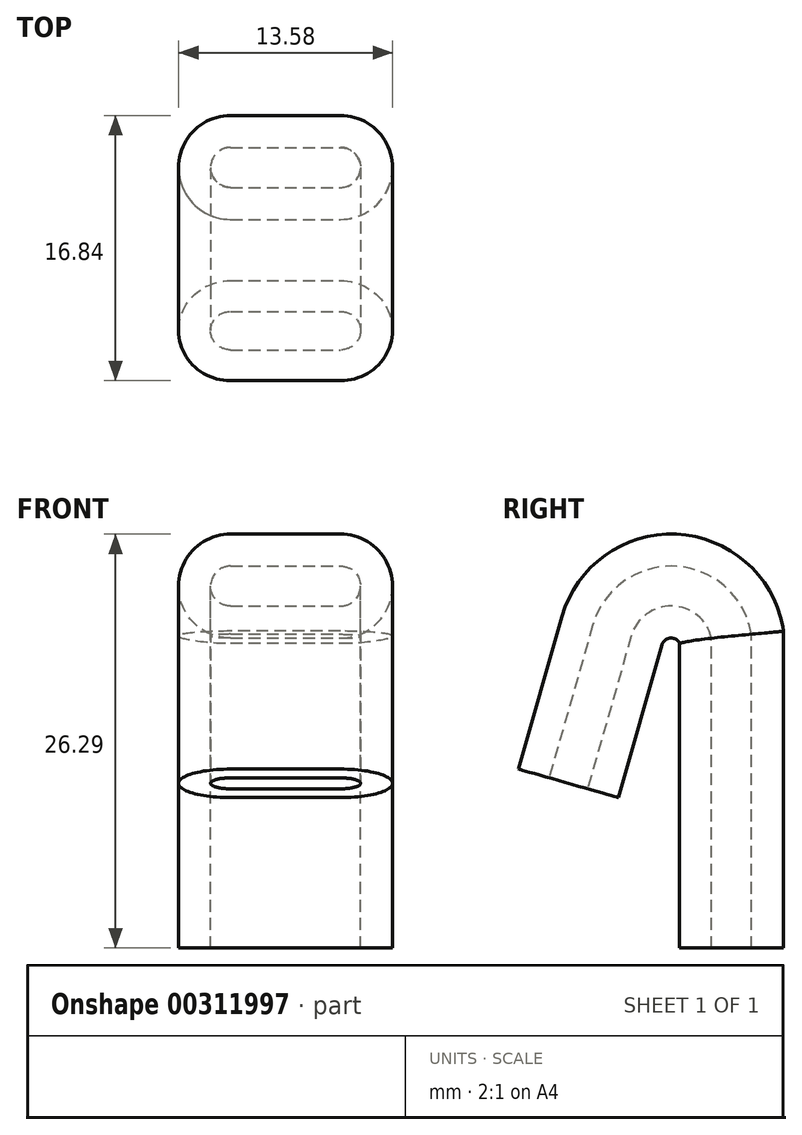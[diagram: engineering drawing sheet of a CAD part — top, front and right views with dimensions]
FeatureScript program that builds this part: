
annotation { "Feature Type Name" : "Feature", "Feature Type Description" : "" }
export const myFeature = defineFeature(function(context is Context, id is Id, definition is map)
    precondition{}
    {
        {
            var Q0;
            Q0=qCreatedBy(makeId("Right.planeOp"),FACE);
            var sketch = newSketch(context, id + "F0", { "sketchPlane" : qUnion([Q0])});
            skLineSegment(sketch, "E0", {"start": v(0, 0) * mm, "end": v(0, 19.81) * mm});
            skLineSegment(sketch, "E1", {"start": v(-5.08, 24.9) * mm, "end": v(-7.6, 24.9) * mm});
            skLineSegment(sketch, "E2", {"start": v(-12.48, 21.2) * mm, "end": v(-15.24, 11.54) * mm});
            skPoint(sketch, "E3.visualSharp", {"position": v(-11.43, 24.9) * mm});
            skArc(sketch, "E3.filletArc", {"start": v(-7.6, 24.9) * mm, "mid": v(-10.66, 23.87) * mm, "end": v(-12.48, 21.2) * mm});
            skPoint(sketch, "E4.visualSharp", {"position": v(0, 24.9) * mm});
            skArc(sketch, "E4.filletArc", {"start": v(0, 19.81) * mm, "mid": v(-1.49, 23.4) * mm, "end": v(-5.08, 24.9) * mm});
            skLineSegment(sketch, "E5.0", {"start": v(-10.14, 20.15) * mm, "end": v(-12.9, 10.46) * mm});
            skLineSegment(sketch, "E6.0", {"start": v(-2.54, 0) * mm, "end": v(-2.54, 19.81) * mm});
            skPoint(sketch, "E7.visualSharp", {"position": v(-9.56, 22.17) * mm});
            skPoint(sketch, "E8.visualSharp", {"position": v(-2.54, 22.35) * mm});
            skArc(sketch, "E9", {"start": v(-2.54, 19.81) * mm, "mid": v(-6.2, 22.99) * mm, "end": v(-10.14, 20.15) * mm});
            skSolve(sketch);
        }
        {
            var Q0;
            Q0=sQuery(id+"F0.wireOp",EDGE,"E6.0");
            var Q1;
            Q1=sQuery(id+"F0.wireOp",VERTEX,"E6.0.start");
            cPlane(context, id + "F1", {"entities" : qUnion([Q0, Q1]), "cplaneType" : CPlaneType.LINE_POINT, "offset" : 25.4 * mm, "width" : 152.4 * mm, "height" : 152.4 * mm});
        }
        {
            var Q0;
            Q0=qCreatedBy(id+"F1.planeOp",FACE);
            var sketch = newSketch(context, id + "F2", { "sketchPlane" : qUnion([Q0])});
            skLineSegment(sketch, "E10.bottom", {"start": v(-3.5, -3.81) * mm, "end": v(3.5, -3.81) * mm});
            skLineSegment(sketch, "E10.top", {"start": v(-3.5, -1.27) * mm, "end": v(3.5, -1.27) * mm});
            skLineSegment(sketch, "E10.left", {"start": v(-4.76, -2.54) * mm, "end": v(-4.76, -2.54) * mm});
            skLineSegment(sketch, "E10.right", {"start": v(4.76, -2.54) * mm, "end": v(4.76, -2.54) * mm});
            skPoint(sketch, "E11.visualSharp", {"position": v(4.76, -3.81) * mm});
            skArc(sketch, "E11.filletArc", {"start": v(3.5, -3.81) * mm, "mid": v(4.4, -3.44) * mm, "end": v(4.76, -2.54) * mm});
            skPoint(sketch, "E12.visualSharp", {"position": v(4.76, -1.27) * mm});
            skArc(sketch, "E12.filletArc", {"start": v(4.76, -2.54) * mm, "mid": v(4.4, -1.64) * mm, "end": v(3.5, -1.27) * mm});
            skPoint(sketch, "E13.visualSharp", {"position": v(-4.76, -3.81) * mm});
            skArc(sketch, "E13.filletArc", {"start": v(-4.76, -2.54) * mm, "mid": v(-4.4, -3.44) * mm, "end": v(-3.5, -3.81) * mm});
            skPoint(sketch, "E14.visualSharp", {"position": v(-4.76, -1.27) * mm});
            skArc(sketch, "E14.filletArc", {"start": v(-3.5, -1.27) * mm, "mid": v(-4.4, -1.64) * mm, "end": v(-4.76, -2.54) * mm});
            skLineSegment(sketch, "E15", {"start": v(-4.76, -2.54) * mm, "end": v(4.76, -2.54) * mm});
            skArc(sketch, "E16.0", {"start": v(-6.8, -2.54) * mm, "mid": v(-5.83, -4.87) * mm, "end": v(-3.5, -5.84) * mm});
            skArc(sketch, "E16.1", {"start": v(3.5, -5.84) * mm, "mid": v(5.83, -4.87) * mm, "end": v(6.8, -2.54) * mm});
            skArc(sketch, "E16.2", {"start": v(6.8, -2.54) * mm, "mid": v(5.83, -0.2) * mm, "end": v(3.5, 0.76) * mm});
            skLineSegment(sketch, "E16.3", {"start": v(-3.5, -5.84) * mm, "end": v(3.5, -5.84) * mm});
            skLineSegment(sketch, "E16.4", {"start": v(-3.5, 0.76) * mm, "end": v(3.5, 0.76) * mm});
            skArc(sketch, "E16.5", {"start": v(-3.5, 0.76) * mm, "mid": v(-5.83, -0.2) * mm, "end": v(-6.8, -2.54) * mm});
            skSolve(sketch);
        }
        {
            var Q0;
            Q0=makeQuery(id+"F2.imprint","IMPRINT",FACE,{"disambiguationData":[TD([[makeQuery(id+"F2.imprint","IMPRINT",EDGE,{"derivedFrom":sQuery(id+"F2.wireOp",EDGE,"E10.bottom")}),-1.0]])]});
            var Q1;
            Q1=sQuery(id+"F0.wireOp",EDGE,"E9");
            var Q2;
            Q2=sQuery(id+"F0.wireOp",EDGE,"E6.0");
            var Q3;
            Q3=sQuery(id+"F0.wireOp",EDGE,"E5.0");
            sweep(context, id + "F3", {"profiles" : qUnion([Q0]), "path" : qUnion([Q1, Q2, Q3])});
        }
        {
            var Q0;
            Q0=makeQuery(id+"F3.opSweep","CAP_FACE",FACE,{"disambiguationData":[OSD([sQuery(id+"F0.wireOp",VERTEX,"E6.0.start"),sQuery(id+"F2.wireOp",EDGE,"E10.bottom"),sQuery(id+"F2.wireOp",EDGE,"E10.top"),sQuery(id+"F2.wireOp",EDGE,"E11.filletArc"),sQuery(id+"F2.wireOp",EDGE,"E12.filletArc"),sQuery(id+"F2.wireOp",EDGE,"E13.filletArc"),sQuery(id+"F2.wireOp",EDGE,"E14.filletArc"),sQuery(id+"F2.wireOp",EDGE,"E16.0"),sQuery(id+"F2.wireOp",EDGE,"E16.1"),sQuery(id+"F2.wireOp",EDGE,"E16.2"),sQuery(id+"F2.wireOp",EDGE,"E16.3"),sQuery(id+"F2.wireOp",EDGE,"E16.4"),sQuery(id+"F2.wireOp",EDGE,"E16.5")])],"isStart":true});
            cPlane(context, id + "F4", {"entities" : qUnion([Q0]), "cplaneType" : CPlaneType.OFFSET, "offset" : 25.4 * mm, "width" : 152.4 * mm, "height" : 152.4 * mm});
        }
    });
